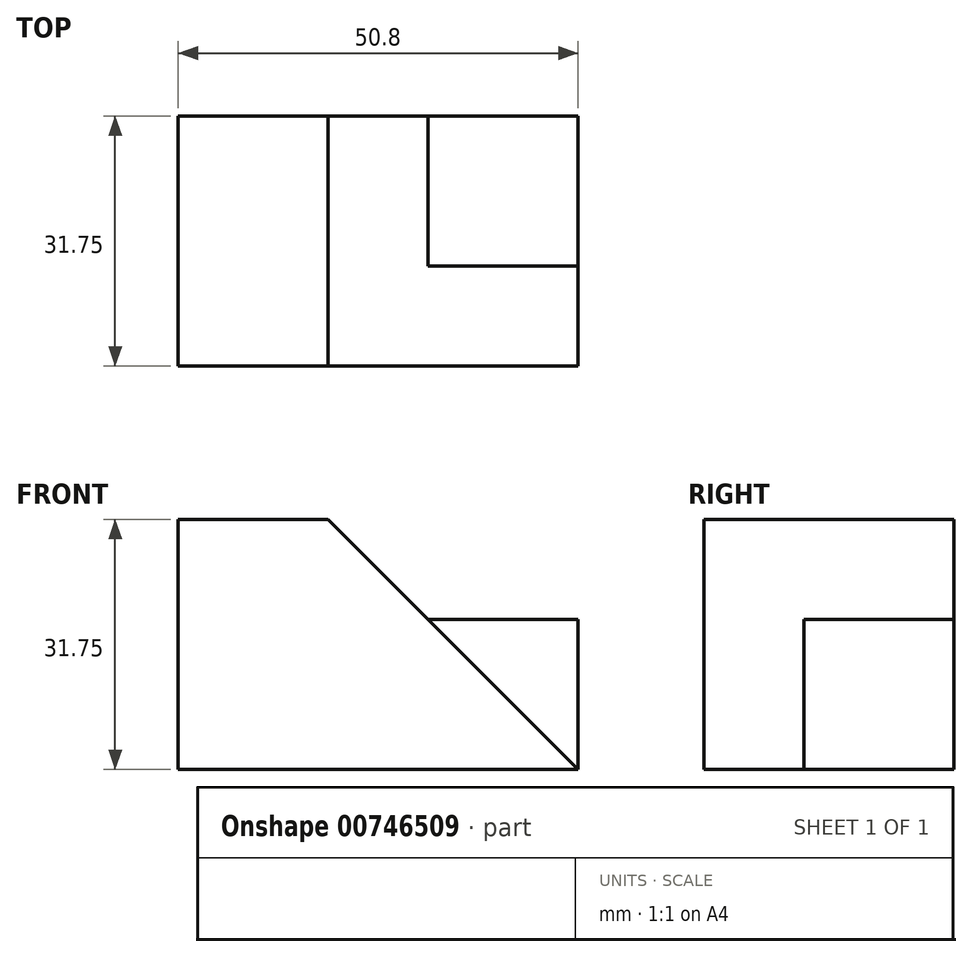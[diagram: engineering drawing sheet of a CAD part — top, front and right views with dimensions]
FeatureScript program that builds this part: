
annotation { "Feature Type Name" : "Feature", "Feature Type Description" : "" }
export const myFeature = defineFeature(function(context is Context, id is Id, definition is map)
    precondition{}
    {
        {
            var Q0;
            Q0=qCreatedBy(makeId("Front.planeOp"),FACE);
            var sketch = newSketch(context, id + "F0", { "sketchPlane" : qUnion([Q0])});
            skLineSegment(sketch, "E0", {"start": v(0, 0) * mm, "end": v(0, 31.75) * mm});
            skLineSegment(sketch, "E1", {"start": v(0, 31.75) * mm, "end": v(50.8, 31.75) * mm});
            skLineSegment(sketch, "E2", {"start": v(50.8, 31.75) * mm, "end": v(50.8, 0) * mm});
            skLineSegment(sketch, "E3", {"start": v(50.8, 0) * mm, "end": v(0, 0) * mm});
            skSolve(sketch);
        }
        {
            var Q0;
            Q0=makeQuery(id+"F0.imprint","IMPRINT",FACE,{"disambiguationData":[TD([[makeQuery(id+"F0.imprint","IMPRINT",EDGE,{"derivedFrom":sQuery(id+"F0.wireOp",EDGE,"E0")}),-1.0]])]});
            extrude(context, id + "F1", {"entities" : qUnion([Q0]), "depth" : 25.4 * mm, "offsetDistance" : 25.4 * mm});
        }
        {
            var Q0;
            Q0=makeQuery(id+"F1.opExtrude","CAP_FACE",FACE,{"disambiguationData":[OSD([sQuery(id+"F0.wireOp",EDGE,"E0"),sQuery(id+"F0.wireOp",EDGE,"E1"),sQuery(id+"F0.wireOp",EDGE,"E2"),sQuery(id+"F0.wireOp",EDGE,"E3")])],"isStart":false});
            var sketch = newSketch(context, id + "F2", { "sketchPlane" : qUnion([Q0])});
            skLineSegment(sketch, "E4", {"start": v(50.8, 0) * mm, "end": v(19.05, 31.75) * mm});
            skLineSegment(sketch, "E5", {"start": v(19.05, 31.75) * mm, "end": v(50.8, 31.75) * mm});
            skSolve(sketch);
        }
        {
            var Q0;
            Q0=makeQuery(id+"F2.imprint","IMPRINT",FACE,{"disambiguationData":[TD([[makeQuery(id+"F2.imprint","IMPRINT",EDGE,{"derivedFrom":sQuery(id+"F2.wireOp",EDGE,"E4")}),-1.0]])]});
            extrude(context, id + "F3", {"entities" : qUnion([Q0]), "operationType" : NewBodyOperationType.REMOVE, "oppositeDirection" : true, "depth" : 12.7 * mm, "offsetDistance" : 25.4 * mm});
        }
        {
            var Q0;
            Q0=makeQuery(id+"F1.opExtrude","CAP_FACE",FACE,{"disambiguationData":[OSD([sQuery(id+"F0.wireOp",EDGE,"E0"),sQuery(id+"F0.wireOp",EDGE,"E1"),sQuery(id+"F0.wireOp",EDGE,"E2"),sQuery(id+"F0.wireOp",EDGE,"E3")])],"isStart":true});
            extrude(context, id + "F4", {"entities" : qUnion([Q0]), "operationType" : NewBodyOperationType.ADD, "depth" : 6.35 * mm, "offsetDistance" : 25.4 * mm});
        }
        {
            var Q0;
            Q0=makeQuery(id+"F3.boolean.opBoolean","COPY",FACE,{"derivedFrom":makeQuery(id+"F3.opExtrude","CAP_FACE",FACE,{"disambiguationData":[OSD([sQuery(id+"F0.wireOp",EDGE,"E2"),sQuery(id+"F2.wireOp",EDGE,"E4"),sQuery(id+"F2.wireOp",EDGE,"E5")])],"isStart":false})});
            var sketch = newSketch(context, id + "F5", { "sketchPlane" : qUnion([Q0])});
            skLineSegment(sketch, "E6", {"start": v(50.8, 15.88) * mm, "end": v(50.8, 15.88) * mm});
            skLineSegment(sketch, "E7", {"start": v(50.8, 15.88) * mm, "end": v(50.8, 19.05) * mm});
            skLineSegment(sketch, "E8", {"start": v(50.8, 19.05) * mm, "end": v(50.8, 19.05) * mm});
            skLineSegment(sketch, "E9", {"start": v(50.8, 19.05) * mm, "end": v(50.8, 15.88) * mm});
            skLineSegment(sketch, "E10", {"start": v(50.8, 19.05) * mm, "end": v(31.75, 19.05) * mm});
            skLineSegment(sketch, "E11", {"start": v(31.75, 19.05) * mm, "end": v(19.05, 31.75) * mm});
            skLineSegment(sketch, "E12", {"start": v(19.05, 31.75) * mm, "end": v(50.8, 31.75) * mm});
            skLineSegment(sketch, "E13", {"start": v(50.8, 31.75) * mm, "end": v(50.8, 19.05) * mm});
            skSolve(sketch);
        }
        {
            var Q0;
            Q0 = qSketchRegion(id + "F5", true);
            extrude(context, id + "F6", {"entities" : qUnion([Q0]), "operationType" : NewBodyOperationType.ADD, "depth" : 25.4 * mm, "offsetDistance" : 25.4 * mm});
        }
        {
            var Q0;
            Q0=makeQuery(id+"F6.opExtrude","CAP_FACE",FACE,{"disambiguationData":[OSD([sQuery(id+"F5.wireOp",EDGE,"E10"),sQuery(id+"F5.wireOp",EDGE,"E11"),sQuery(id+"F5.wireOp",EDGE,"E12"),sQuery(id+"F5.wireOp",EDGE,"E13")])],"isStart":false});
            extrude(context, id + "F7", {"entities" : qUnion([Q0]), "operationType" : NewBodyOperationType.REMOVE, "oppositeDirection" : true, "depth" : 50.8 * mm, "offsetDistance" : 25.4 * mm});
        }
    });
